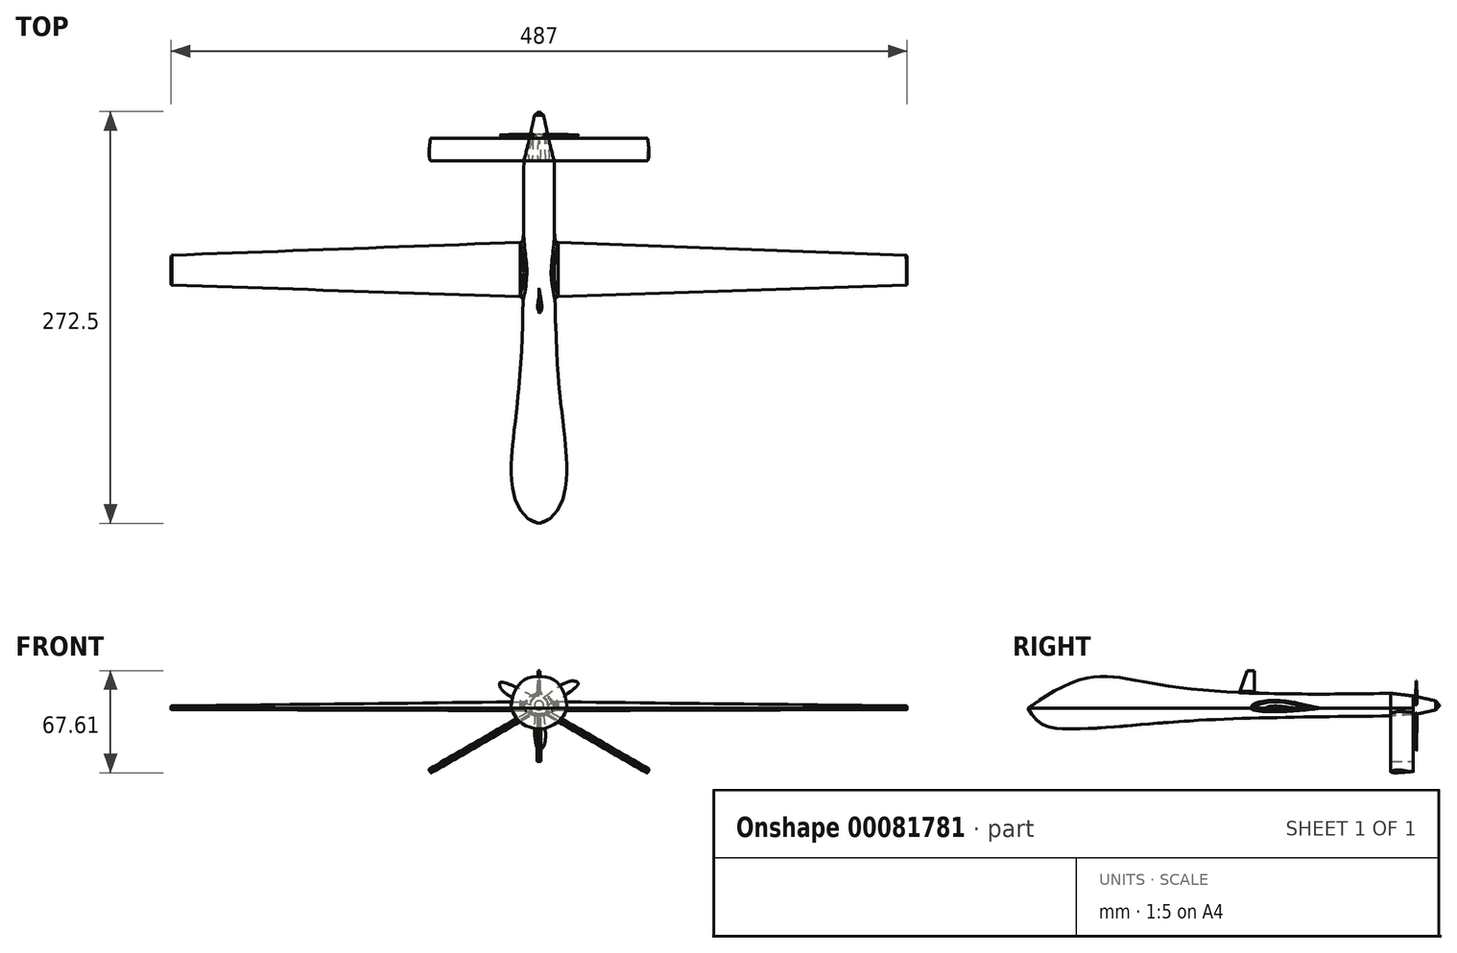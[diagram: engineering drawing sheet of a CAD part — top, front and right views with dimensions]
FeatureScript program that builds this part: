
annotation { "Feature Type Name" : "Feature", "Feature Type Description" : "" }
export const myFeature = defineFeature(function(context is Context, id is Id, definition is map)
    precondition{}
    {
        {
            var Q0;
            Q0=qCreatedBy(makeId("Right.planeOp"),FACE);
            var sketch = newSketch(context, id + "F0", { "sketchPlane" : qUnion([Q0])});
            skLineSegment(sketch, "E0", {"start": v(0, 0) * mm, "end": v(240, 0) * mm});
            skFitSpline(sketch, "E1", {"points": [v(0, 0) * mm, v(37.5, 19.82) * mm, v(94.65, 14.48) * mm, v(240, 10) * mm], "startDerivative": vector(93.49, 65.35) * mm, "endDerivative": vector(326.63, 5.9) * mm});
            skLineSegment(sketch, "E2", {"start": v(240, 10) * mm, "end": v(240, 0) * mm});
            skSolve(sketch);
        }
        {
            var Q0;
            Q0=qCreatedBy(makeId("Front.planeOp"),FACE);
            cPlane(context, id + "F1", {"entities" : qUnion([Q0]), "cplaneType" : CPlaneType.OFFSET, "offset" : 240 * mm, "oppositeDirection" : true, "width" : 150 * mm, "height" : 150 * mm});
        }
        {
            var Q0;
            Q0=qCreatedBy(id+"F1.planeOp",FACE);
            var sketch = newSketch(context, id + "F2", { "sketchPlane" : qUnion([Q0])});
            skArc(sketch, "E3", {"start": v(10, 0) * mm, "mid": v(0, 10) * mm, "end": v(-10, 0) * mm});
            skLineSegment(sketch, "E4", {"start": v(-10, 0) * mm, "end": v(10, 0) * mm});
            skPoint(sketch, "E5.0.start.orphan", {"position": v(0, 10) * mm});
            skSolve(sketch);
        }
        {
            var Q0;
            Q0=qCreatedBy(makeId("Top.planeOp"),FACE);
            var sketch = newSketch(context, id + "F3", { "sketchPlane" : qUnion([Q0])});
            skLineSegment(sketch, "E6", {"start": v(0, 0) * mm, "end": v(0, 272.56) * mm, "construction": true});
            skFitSpline(sketch, "E7.0", {"points": [v(0, 240) * mm, v(-3.33, 240) * mm, v(-6.67, 240) * mm, v(-10, 240) * mm]});
            skFitSpline(sketch, "E8", {"points": [v(-10, 240) * mm, v(-13.37, 88.04) * mm, v(-16.88, 19.92) * mm, v(0, 0) * mm], "startDerivative": vector(-2.86, -342.32) * mm, "endDerivative": vector(133.74, -24.52) * mm});
            skFitSpline(sketch, "E9.MirrorCS", {"points": [v(10, 240) * mm, v(13.37, 88.04) * mm, v(16.88, 19.92) * mm, v(0, 0) * mm], "startDerivative": vector(2.86, -342.32) * mm, "endDerivative": vector(-133.74, -24.52) * mm});
            skSolve(sketch);
        }
        {
            var Q0;
            Q0=qCreatedBy(makeId("Front.planeOp"),FACE);
            cPlane(context, id + "F4", {"entities" : qUnion([Q0]), "cplaneType" : CPlaneType.OFFSET, "offset" : 37.5 * mm, "oppositeDirection" : true, "width" : 150 * mm, "height" : 150 * mm});
        }
        {
            var Q0;
            Q0=qCreatedBy(id+"F4.planeOp",FACE);
            var sketch = newSketch(context, id + "F5", { "sketchPlane" : qUnion([Q0])});
            skArc(sketch, "E10", {"start": v(18.28, 0) * mm, "mid": v(0, 19.82) * mm, "end": v(-18.28, 0) * mm});
            skLineSegment(sketch, "E11", {"start": v(-18.28, 0) * mm, "end": v(18.28, 0) * mm});
            skSolve(sketch);
        }
        {
            var Q0;
            Q0=qCreatedBy(makeId("Front.planeOp"),FACE);
            cPlane(context, id + "F6", {"entities" : qUnion([Q0]), "cplaneType" : CPlaneType.OFFSET, "offset" : 150 * mm, "oppositeDirection" : true, "width" : 150 * mm, "height" : 150 * mm});
        }
        {
            var Q0;
            Q0=qCreatedBy(id+"F6.planeOp",FACE);
            var sketch = newSketch(context, id + "F7", { "sketchPlane" : qUnion([Q0])});
            skArc(sketch, "E12", {"start": v(10.54, 0) * mm, "mid": v(0, 10.12) * mm, "end": v(-10.54, 0) * mm});
            skLineSegment(sketch, "E13", {"start": v(-10.54, 0) * mm, "end": v(10.54, 0) * mm});
            skSolve(sketch);
        }
        {
            var Q0;
            Q0=makeQuery(id+"F2.imprint","IMPRINT",FACE,{"disambiguationData":[TD([[makeQuery(id+"F2.imprint","IMPRINT",EDGE,{"derivedFrom":sQuery(id+"F2.wireOp",EDGE,"E3")}),1.0]])]});
            var Q1;
            Q1=makeQuery(id+"F7.imprint","IMPRINT",FACE,{"disambiguationData":[TD([[makeQuery(id+"F7.imprint","IMPRINT",EDGE,{"derivedFrom":sQuery(id+"F7.wireOp",EDGE,"E12")}),1.0]])]});
            var Q2;
            Q2=makeQuery(id+"F5.imprint","IMPRINT",FACE,{"disambiguationData":[TD([[makeQuery(id+"F5.imprint","IMPRINT",EDGE,{"derivedFrom":sQuery(id+"F5.wireOp",EDGE,"E10")}),1.0]])]});
            var Q3;
            Q3=sQuery(id+"F3.wireOp",VERTEX,"E9.MirrorCS.3.internal");
            var Q4;
            Q4=sQuery(id+"F0.wireOp",EDGE,"E1");
            var Q5;
            Q5=sQuery(id+"F3.wireOp",EDGE,"E9.MirrorCS");
            var Q6;
            Q6=sQuery(id+"F3.wireOp",EDGE,"E8");
            loft(context, id + "F8", {"addGuides" : true, "sheetProfilesArray" : [{ "sheetProfileEntities" : qUnion([Q0]) }, { "sheetProfileEntities" : qUnion([Q1]) }, { "sheetProfileEntities" : qUnion([Q2]) }, { "sheetProfileEntities" : qUnion([Q3]) }], "guidesArray" : [{ "guideEntities" : qUnion([Q4]), "guideDerivativeType" : LoftGuideDerivativeType.DEFAULT, "guideDerivativeMagnitude" : 1 }, { "guideEntities" : qUnion([Q5]), "guideDerivativeType" : LoftGuideDerivativeType.DEFAULT, "guideDerivativeMagnitude" : 1 }, { "guideEntities" : qUnion([Q6]), "guideDerivativeType" : LoftGuideDerivativeType.DEFAULT, "guideDerivativeMagnitude" : 1 }]});
        }
        {
            var Q0;
            Q0=qCreatedBy(makeId("Right.planeOp"),FACE);
            var sketch = newSketch(context, id + "F9", { "sketchPlane" : qUnion([Q0])});
            skPoint(sketch, "E14.0", {"position": v(240, 0) * mm});
            skFitSpline(sketch, "E15", {"points": [v(0, 0) * mm, v(16.5, -12.8) * mm, v(84.8, -9.9) * mm, v(240, -5) * mm], "startDerivative": vector(89.7, -143.98) * mm, "endDerivative": vector(544.57, 5.36) * mm});
            skLineSegment(sketch, "E16", {"start": v(0, 0) * mm, "end": v(240, 0) * mm});
            skSolve(sketch);
        }
        {
            var Q0;
            Q0=qCreatedBy(id+"F1.planeOp",FACE);
            var sketch = newSketch(context, id + "F10", { "sketchPlane" : qUnion([Q0])});
            skFitSpline(sketch, "E17.0", {"points": [v(0, 0) * mm, v(-3.33, 0) * mm, v(-6.67, 0) * mm, v(-10, 0) * mm]});
            skLineSegment(sketch, "E18.0", {"start": v(-10, 0) * mm, "end": v(10, 0) * mm});
            skArc(sketch, "E19", {"start": v(-10, 0) * mm, "mid": v(0, -5) * mm, "end": v(10, 0) * mm});
            skSolve(sketch);
        }
        {
            var Q0;
            Q0=qCreatedBy(id+"F6.planeOp",FACE);
            var sketch = newSketch(context, id + "F11", { "sketchPlane" : qUnion([Q0])});
            skArc(sketch, "E20", {"start": v(-10.54, 0) * mm, "mid": v(0, -6.4) * mm, "end": v(10.54, 0) * mm});
            skLineSegment(sketch, "E21", {"start": v(10.54, 0) * mm, "end": v(-10.54, 0) * mm});
            skSolve(sketch);
        }
        {
            var Q0;
            Q0=qCreatedBy(id+"F4.planeOp",FACE);
            var sketch = newSketch(context, id + "F12", { "sketchPlane" : qUnion([Q0])});
            skArc(sketch, "E22", {"start": v(-18.28, 0) * mm, "mid": v(0, -13.44) * mm, "end": v(18.28, 0) * mm});
            skLineSegment(sketch, "E23", {"start": v(-18.28, 0) * mm, "end": v(18.28, 0) * mm});
            skSolve(sketch);
        }
        {
            var Q1;
            {var subQ0=sQuery(id+"F10.wireOp",EDGE,"E19");Q1=makeQuery(id+"F10.imprint","IMPRINT",FACE,{"disambiguationData":[TD([[makeQuery(id+"F10.imprint","IMPRINT",EDGE,{"derivedFrom":subQ0}),1.0]])]});}
            var Q2;
            Q2=makeQuery(id+"F11.imprint","IMPRINT",FACE,{"disambiguationData":[TD([[makeQuery(id+"F11.imprint","IMPRINT",EDGE,{"derivedFrom":sQuery(id+"F11.wireOp",EDGE,"E20")}),1.0]])]});
            var Q3;
            Q3=makeQuery(id+"F12.imprint","IMPRINT",FACE,{"disambiguationData":[TD([[makeQuery(id+"F12.imprint","IMPRINT",EDGE,{"derivedFrom":sQuery(id+"F12.wireOp",EDGE,"E22")}),1.0]])]});
            var Q4;
            Q4=sQuery(id+"F9.wireOp",VERTEX,"E15.0.internal");
            var Q5;
            Q5=sQuery(id+"F3.wireOp",EDGE,"E8");
            var Q6;
            Q6=sQuery(id+"F3.wireOp",EDGE,"E9.MirrorCS");
            var Q7;
            Q7=sQuery(id+"F9.wireOp",EDGE,"E15");
            loft(context, id + "F13", {"operationType" : NewBodyOperationType.ADD, "addGuides" : true, "sheetProfilesArray" : [{ "sheetProfileEntities" : qUnion([Q1]) }, { "sheetProfileEntities" : qUnion([Q2]) }, { "sheetProfileEntities" : qUnion([Q3]) }, { "sheetProfileEntities" : qUnion([Q4]) }], "guidesArray" : [{ "guideEntities" : qUnion([Q5]), "guideDerivativeType" : LoftGuideDerivativeType.DEFAULT, "guideDerivativeMagnitude" : 1 }, { "guideEntities" : qUnion([Q6]), "guideDerivativeType" : LoftGuideDerivativeType.DEFAULT, "guideDerivativeMagnitude" : 1 }, { "guideEntities" : qUnion([Q7]), "guideDerivativeType" : LoftGuideDerivativeType.DEFAULT, "guideDerivativeMagnitude" : 1 }]});
        }
        {
            var Q0;
            Q0=qCreatedBy(makeId("Right.planeOp"),FACE);
            var sketch = newSketch(context, id + "F14", { "sketchPlane" : qUnion([Q0])});
            skLineSegment(sketch, "E24", {"start": v(0, 0) * mm, "end": v(150, 0) * mm, "construction": true});
            skLineSegment(sketch, "E25", {"start": v(150, 0) * mm, "end": v(186, 0) * mm, "construction": true});
            skFitSpline(sketch, "E26", {"points": [v(150, 0) * mm, v(162.77, 4.35) * mm, v(186, 0) * mm], "startDerivative": vector(1.89, 17.28) * mm, "endDerivative": vector(43.95, -12.7) * mm});
            skFitSpline(sketch, "E27", {"points": [v(150, 0) * mm, v(161.94, -1.41) * mm, v(186, 0) * mm], "startDerivative": vector(11.14, -7.95) * mm, "endDerivative": vector(52.3, 6.57) * mm});
            skSolve(sketch);
        }
        {
            var Q0;
            Q0 = qSketchRegion(id + "F14", true);
            extrude(context, id + "F15", {"entities" : qUnion([Q0]), "operationType" : NewBodyOperationType.ADD, "endBound" : BoundingType.SYMMETRIC, "depth" : 25 * mm});
        }
        {
            var Q0;
            Q0=qCreatedBy(makeId("Right.planeOp"),FACE);
            cPlane(context, id + "F16", {"entities" : qUnion([Q0]), "cplaneType" : CPlaneType.OFFSET, "offset" : 243.5 * mm, "width" : 150 * mm, "height" : 150 * mm});
        }
        {
            var Q0;
            Q0=qCreatedBy(id+"F16.planeOp",FACE);
            var sketch = newSketch(context, id + "F17", { "sketchPlane" : qUnion([Q0])});
            skFitSpline(sketch, "E28.0.0", {"points": [v(186, 0) * mm, v(177.65, 2.41) * mm, v(165.41, 6.33) * mm, v(150.27, 2.48) * mm, v(150, 0) * mm]});
            skFitSpline(sketch, "E28.0.1", {"points": [v(150, 0) * mm, v(151.54, -1.1) * mm, v(164.41, -1.68) * mm, v(175.78, -1.28) * mm, v(186, 0) * mm]});
            skLineSegment(sketch, "E29", {"start": v(142.65, 0) * mm, "end": v(197.39, 0) * mm, "construction": true});
            skFitSpline(sketch, "E30", {"points": [v(157.7, 0) * mm, v(162.9, 1.58) * mm, v(177.41, 0) * mm], "startDerivative": vector(0.8, 8.3) * mm, "endDerivative": vector(32.19, -4.29) * mm});
            skFitSpline(sketch, "E31", {"points": [v(157.7, 0) * mm, v(164.23, -0.7) * mm, v(177.41, 0) * mm], "startDerivative": vector(2.27, -4.37) * mm, "endDerivative": vector(24.46, 2.77) * mm});
            skSolve(sketch);
        }
        {
            var Q0;
            Q0=makeQuery(id+"F17.imprint","IMPRINT",FACE,{"disambiguationData":[TD([[makeQuery(id+"F17.imprint","IMPRINT",EDGE,{"derivedFrom":sQuery(id+"F17.wireOp",EDGE,"E30")}),-1.0]])]});
            var Q1;
            Q1=makeQuery(id+"F15.opExtrude","CAP_FACE",FACE,{"disambiguationData":[OSD([sQuery(id+"F14.wireOp",EDGE,"E26"),sQuery(id+"F14.wireOp",EDGE,"E27")])],"isStart":false});
            loft(context, id + "F18", {"sheetProfilesArray" : [{ "sheetProfileEntities" : qUnion([Q0]) }, { "sheetProfileEntities" : qUnion([Q1]) }]});
        }
        {
            var Q0;
            {var subQ0=sQuery(id+"F17.wireOp",EDGE,"E30");var subQ1=sQuery(id+"F17.wireOp",EDGE,"E31");Q0=makeQuery(id+"F18.opLoft","MID_CAP_EDGE",EDGE,{"disambiguationData":[OSD([subQ0,subQ1]),TDD([makeQuery(id+"F17.imprint","INTERSECT",VERTEX,{"disambiguationData":[OD(0.0)],"derivedFrom":[subQ0,subQ1]}),makeQuery(id+"F17.imprint","INTERSECT",VERTEX,{"disambiguationData":[OD(1.0)],"derivedFrom":[subQ0,subQ1]}),makeQuery(id+"F17.imprint","IMPRINT",EDGE,{"derivedFrom":subQ0})])],"capPos":0.0});}
            fillet(context, id + "F19", {"entities" : qUnion([Q0]), "radius" : 0.5 * mm, "tangentPropagation" : true, "allowEdgeOverflow" : false});
        }
        {
            var Q0;
            Q0=makeQuery(id+"F18.opLoft","SWEPT_BODY",BODY,{"disambiguationData":[OSD([sQuery(id+"F14.wireOp",EDGE,"E26"),sQuery(id+"F14.wireOp",EDGE,"E27"),makeQuery(id+"F17.imprint","IMPRINT",FACE,{"disambiguationData":[TD([[makeQuery(id+"F17.imprint","IMPRINT",EDGE,{"derivedFrom":sQuery(id+"F17.wireOp",EDGE,"E30")}),-1.0]])]})])]});
            var Q1;
            Q1=qCreatedBy(makeId("Right.planeOp"),FACE);
            mirror(context, id + "F20", {"operationType" : NewBodyOperationType.ADD, "entities" : qUnion([Q0]), "mirrorPlane" : qUnion([Q1])});
        }
        {
            var Q0;
            Q0=qCreatedBy(makeId("Front.planeOp"),FACE);
            cPlane(context, id + "F21", {"entities" : qUnion([Q0]), "cplaneType" : CPlaneType.OFFSET, "offset" : 255 * mm, "oppositeDirection" : true, "width" : 150 * mm, "height" : 150 * mm});
        }
        {
            var Q0;
            Q0=qCreatedBy(id+"F21.planeOp",FACE);
            var sketch = newSketch(context, id + "F22", { "sketchPlane" : qUnion([Q0])});
            skFitSpline(sketch, "E32.0.0", {"points": [v(0, 10) * mm, v(0.66, 10) * mm, v(1.3, 9.94) * mm, v(1.95, 9.8) * mm, v(2.6, 9.68) * mm, v(3.22, 9.5) * mm, v(3.83, 9.24) * mm, v(4.43, 8.99) * mm, v(5, 8.68) * mm, v(5.56, 8.31) * mm, v(6.1, 7.95) * mm, v(6.6, 7.54) * mm, v(7.07, 7.07) * mm, v(7.53, 6.6) * mm, v(7.95, 6.1) * mm, v(8.31, 5.56) * mm, v(8.68, 5.01) * mm, v(8.99, 4.43) * mm, v(9.24, 3.83) * mm, v(9.49, 3.22) * mm, v(9.68, 2.6) * mm, v(9.8, 1.95) * mm, v(9.94, 1.3) * mm, v(10, 0.66) * mm, v(10, 0) * mm]});
            skFitSpline(sketch, "E32.0.1", {"points": [v(10, 0) * mm, v(9.42, -0.78) * mm, v(8.75, -1.47) * mm, v(8, -2.1) * mm, v(7.27, -2.72) * mm, v(6.46, -3.25) * mm, v(5.6, -3.68) * mm, v(4.72, -4.11) * mm, v(3.82, -4.44) * mm, v(2.87, -4.67) * mm, v(1.93, -4.89) * mm, v(0.97, -5) * mm, v(0, -5) * mm]});
            skFitSpline(sketch, "E32.0.2", {"points": [v(0, -5) * mm, v(-0.97, -5) * mm, v(-1.93, -4.89) * mm, v(-2.87, -4.67) * mm, v(-3.82, -4.44) * mm, v(-4.72, -4.11) * mm, v(-5.6, -3.68) * mm, v(-6.46, -3.25) * mm, v(-7.26, -2.72) * mm, v(-8, -2.1) * mm, v(-8.75, -1.48) * mm, v(-9.42, -0.78) * mm, v(-10, 0) * mm]});
            skFitSpline(sketch, "E32.0.3", {"points": [v(-10, 0) * mm, v(-10, 0.66) * mm, v(-9.94, 1.3) * mm, v(-9.8, 1.95) * mm, v(-9.68, 2.6) * mm, v(-9.5, 3.22) * mm, v(-9.24, 3.83) * mm, v(-8.99, 4.43) * mm, v(-8.68, 5) * mm, v(-8.31, 5.56) * mm, v(-7.95, 6.1) * mm, v(-7.54, 6.6) * mm, v(-7.07, 7.07) * mm, v(-6.6, 7.53) * mm, v(-6.1, 7.95) * mm, v(-5.56, 8.31) * mm, v(-5.01, 8.68) * mm, v(-4.43, 8.99) * mm, v(-3.83, 9.24) * mm, v(-3.22, 9.49) * mm, v(-2.6, 9.68) * mm, v(-1.95, 9.8) * mm, v(-1.3, 9.94) * mm, v(-0.66, 10) * mm, v(0, 10) * mm]});
            skCircle(sketch, "E33", {"center": v(0, 2) * mm, "radius": 6.25 * mm});
            skLineSegment(sketch, "E34", {"start": v(10, 0) * mm, "end": v(-10, 0) * mm, "construction": true});
            skPoint(sketch, "E35", {"position": v(5.92, 0) * mm});
            skPoint(sketch, "E36", {"position": v(-5.92, 0) * mm});
            skPoint(sketch, "E37", {"position": v(0, 8.25) * mm});
            skPoint(sketch, "E38", {"position": v(0, -4.25) * mm});
            skSolve(sketch);
        }
        {
            var Q0;
            Q0=qCreatedBy(makeId("Front.planeOp"),FACE);
            cPlane(context, id + "F23", {"entities" : qUnion([Q0]), "cplaneType" : CPlaneType.OFFSET, "offset" : 270 * mm, "oppositeDirection" : true, "width" : 150 * mm, "height" : 150 * mm});
        }
        {
            var Q0;
            Q0=qCreatedBy(makeId("Top.planeOp"),FACE);
            var sketch = newSketch(context, id + "F24", { "sketchPlane" : qUnion([Q0])});
            skPoint(sketch, "E39.0", {"position": v(-10, 240) * mm});
            skPoint(sketch, "E40.0", {"position": v(10, 240) * mm});
            skPoint(sketch, "E41.0", {"position": v(-5.92, 255) * mm});
            skPoint(sketch, "E42.0", {"position": v(5.92, 255) * mm});
            skLineSegment(sketch, "E43", {"start": v(10, 240) * mm, "end": v(5.92, 255) * mm});
            skLineSegment(sketch, "E44", {"start": v(-10, 240) * mm, "end": v(-5.92, 255) * mm});
            skSolve(sketch);
        }
        {
            var Q1;
            {var subQ0=sQuery(id+"F10.wireOp",EDGE,"E19");Q1=makeQuery(id+"F13.boolean.opBoolean","MERGE",FACE,{"derivedFrom":[makeQuery(id+"F8.opLoft","CAP_FACE",FACE,{"disambiguationData":[OSD([makeQuery(id+"F2.imprint","IMPRINT",FACE,{"disambiguationData":[TD([[makeQuery(id+"F2.imprint","IMPRINT",EDGE,{"derivedFrom":sQuery(id+"F2.wireOp",EDGE,"E3")}),1.0]])]})])],"isStart":true}),makeQuery(id+"F13.opLoft","CAP_FACE",FACE,{"disambiguationData":[OSD([makeQuery(id+"F10.imprint","IMPRINT",FACE,{"disambiguationData":[TD([[makeQuery(id+"F10.imprint","IMPRINT",EDGE,{"derivedFrom":subQ0}),1.0]])]})])],"isStart":true})]});}
            var Q2;
            Q2=makeQuery(id+"F22.imprint","IMPRINT",FACE,{"disambiguationData":[TD([[makeQuery(id+"F22.imprint","IMPRINT",EDGE,{"derivedFrom":sQuery(id+"F22.wireOp",EDGE,"E33")}),1.0]])]});
            var Q3;
            Q3=sQuery(id+"F24.wireOp",EDGE,"E44");
            var Q4;
            Q4=sQuery(id+"F24.wireOp",EDGE,"E43");
            loft(context, id + "F25", {"operationType" : NewBodyOperationType.ADD, "addGuides" : true, "sheetProfilesArray" : [{ "sheetProfileEntities" : qUnion([Q1]) }, { "sheetProfileEntities" : qUnion([Q2]) }], "guidesArray" : [{ "guideEntities" : qUnion([Q3]), "guideDerivativeType" : LoftGuideDerivativeType.DEFAULT, "guideDerivativeMagnitude" : 1 }, { "guideEntities" : qUnion([Q4]), "guideDerivativeType" : LoftGuideDerivativeType.DEFAULT, "guideDerivativeMagnitude" : 1 }]});
        }
        {
            var Q0;
            Q0=qCreatedBy(id+"F23.planeOp",FACE);
            var sketch = newSketch(context, id + "F26", { "sketchPlane" : qUnion([Q0])});
            skCircle(sketch, "E45", {"center": v(0, 2) * mm, "radius": 3 * mm});
            skSolve(sketch);
        }
        {
            var Q1;
            Q1=makeQuery(id+"F25.opLoft","CAP_FACE",FACE,{"disambiguationData":[OSD([makeQuery(id+"F22.imprint","IMPRINT",FACE,{"disambiguationData":[TD([[makeQuery(id+"F22.imprint","IMPRINT",EDGE,{"derivedFrom":sQuery(id+"F22.wireOp",EDGE,"E33")}),1.0]])]})])],"isStart":true});
            var Q2;
            Q2=makeQuery(id+"F26.imprint","IMPRINT",FACE,{"disambiguationData":[TD([[makeQuery(id+"F26.imprint","IMPRINT",EDGE,{"derivedFrom":sQuery(id+"F26.wireOp",EDGE,"E45")}),1.0]])]});
            loft(context, id + "F27", {"operationType" : NewBodyOperationType.ADD, "sheetProfilesArray" : [{ "sheetProfileEntities" : qUnion([Q1]) }, { "sheetProfileEntities" : qUnion([Q2]) }]});
        }
        {
            var Q0;
            Q0=qCreatedBy(makeId("Front.planeOp"),FACE);
            cPlane(context, id + "F28", {"entities" : qUnion([Q0]), "cplaneType" : CPlaneType.OFFSET, "offset" : 272.5 * mm, "oppositeDirection" : true, "width" : 150 * mm, "height" : 150 * mm});
        }
        {
            var Q0;
            Q0=qCreatedBy(id+"F28.planeOp",FACE);
            var sketch = newSketch(context, id + "F29", { "sketchPlane" : qUnion([Q0])});
            skFitSpline(sketch, "E46.0.0", {"points": [v(3, 2) * mm, v(3, 1.6) * mm, v(2.92, 1.22) * mm, v(2.77, 0.85) * mm, v(2.62, 0.49) * mm, v(2.4, 0.16) * mm, v(2.12, -0.12) * mm, v(1.84, -0.4) * mm, v(1.52, -0.62) * mm, v(1.15, -0.77) * mm, v(0.78, -0.92) * mm, v(0.4, -1) * mm, v(0, -1) * mm]});
            skFitSpline(sketch, "E46.0.1", {"points": [v(0, -1) * mm, v(-0.4, -1) * mm, v(-0.78, -0.92) * mm, v(-1.15, -0.77) * mm, v(-1.51, -0.62) * mm, v(-1.84, -0.4) * mm, v(-2.12, -0.12) * mm, v(-2.4, 0.16) * mm, v(-2.62, 0.48) * mm, v(-2.77, 0.85) * mm, v(-2.92, 1.22) * mm, v(-3, 1.6) * mm, v(-3, 2) * mm]});
            skFitSpline(sketch, "E46.0.2", {"points": [v(-3, 2) * mm, v(-3, 2.4) * mm, v(-2.92, 2.78) * mm, v(-2.77, 3.15) * mm, v(-2.62, 3.51) * mm, v(-2.4, 3.84) * mm, v(-2.12, 4.12) * mm, v(-1.84, 4.4) * mm, v(-1.52, 4.62) * mm, v(-1.15, 4.77) * mm, v(-0.78, 4.92) * mm, v(-0.4, 5) * mm, v(0, 5) * mm]});
            skFitSpline(sketch, "E46.0.3", {"points": [v(0, 5) * mm, v(0.4, 5) * mm, v(0.78, 4.92) * mm, v(1.15, 4.77) * mm, v(1.51, 4.62) * mm, v(1.84, 4.4) * mm, v(2.12, 4.12) * mm, v(2.4, 3.84) * mm, v(2.62, 3.52) * mm, v(2.77, 3.15) * mm, v(2.92, 2.78) * mm, v(3, 2.4) * mm, v(3, 2) * mm]});
            skPoint(sketch, "E47", {"position": v(0, 2) * mm});
            skSolve(sketch);
        }
        {
            var Q1;
            Q1=makeQuery(id+"F27.opLoft","CAP_FACE",FACE,{"disambiguationData":[OSD([makeQuery(id+"F26.imprint","IMPRINT",FACE,{"disambiguationData":[TD([[makeQuery(id+"F26.imprint","IMPRINT",EDGE,{"derivedFrom":sQuery(id+"F26.wireOp",EDGE,"E45")}),1.0]])]})])],"isStart":true});
            var Q2;
            Q2=sQuery(id+"F29.wireOp",VERTEX,"E47");
            loft(context, id + "F30", {"operationType" : NewBodyOperationType.ADD, "sheetProfilesArray" : [{ "sheetProfileEntities" : qUnion([Q1]) }, { "sheetProfileEntities" : qUnion([Q2]) }]});
        }
        {
            var Q0;
            Q0=qCreatedBy(makeId("Right.planeOp"),FACE);
            cPlane(context, id + "F31", {"entities" : qUnion([Q0]), "cplaneType" : CPlaneType.OFFSET, "offset" : 72 * mm, "width" : 150 * mm, "height" : 150 * mm});
        }
        {
            var Q0;
            Q0=qCreatedBy(id+"F31.planeOp",FACE);
            var sketch = newSketch(context, id + "F32", { "sketchPlane" : qUnion([Q0])});
            skLineSegment(sketch, "E48", {"start": v(0, 0) * mm, "end": v(0, -42) * mm, "construction": true});
            skLineSegment(sketch, "E49", {"start": v(0, -42) * mm, "end": v(271.23, -42) * mm});
            skSolve(sketch);
        }
        {
            assignVariable(context, id + "F33", {"name" : "angle", "anyValue" : 120});
        }
        {
            var Q0;
            Q0=sQuery(id+"F32.wireOp",EDGE,"E49");
            cPlane(context, id + "F34", {"entities" : qUnion([Q0]), "cplaneType" : CPlaneType.LINE_ANGLE, "offset" : 150 * mm, "angle" : (getVariable(context, 'angle')) * degree, "width" : 150 * mm, "height" : 150 * mm});
        }
        {
            var Q0;
            Q0=qCreatedBy(id+"F34.planeOp",FACE);
            var sketch = newSketch(context, id + "F35", { "sketchPlane" : qUnion([Q0])});
            skFitSpline(sketch, "E50.0", {"points": [v(240, 5) * mm, v(245, 4.32) * mm, v(250, 3.64) * mm, v(255, 2.96) * mm], "construction": true});
            skLineSegment(sketch, "E51.0", {"start": v(0, -0.37) * mm, "end": v(242.6, -0.37) * mm, "construction": true});
            skPoint(sketch, "E52.orphan", {"position": v(271.23, -0.37) * mm});
            skFitSpline(sketch, "E53", {"points": [v(240, -0.37) * mm, v(244.56, 1.55) * mm, v(255, -0.37) * mm], "startDerivative": vector(6.04, 10.7) * mm, "endDerivative": vector(29.02, -7.53) * mm});
            skFitSpline(sketch, "E54", {"points": [v(240, -0.37) * mm, v(244.42, -1.27) * mm, v(255, -0.37) * mm], "startDerivative": vector(3.63, -7.22) * mm, "endDerivative": vector(30.34, 2.29) * mm});
            skSolve(sketch);
        }
        {
            var Q0;
            Q0=makeQuery(id+"F35.imprint","IMPRINT",FACE,{"disambiguationData":[TD([[makeQuery(id+"F35.imprint","IMPRINT",EDGE,{"derivedFrom":sQuery(id+"F35.wireOp",EDGE,"E53")}),-1.0]])]});
            extrude(context, id + "F36", {"entities" : qUnion([Q0]), "oppositeDirection" : true, "depth" : 80 * mm});
        }
        {
            var Q0;
            Q0=makeQuery(id+"F36.opExtrude","CAP_EDGE",EDGE,{"disambiguationData":[OSD([sQuery(id+"F35.wireOp",EDGE,"E53")])],"isStart":true});
            var Q1;
            Q1=makeQuery(id+"F36.opExtrude","CAP_EDGE",EDGE,{"disambiguationData":[OSD([sQuery(id+"F35.wireOp",EDGE,"E54")])],"isStart":true});
            fillet(context, id + "F37", {"entities" : qUnion([Q0, Q1]), "radius" : 0.5 * mm, "tangentPropagation" : true, "allowEdgeOverflow" : false});
        }
        {
            var Q0;
            Q0=makeQuery(id+"F36.opExtrude","SWEPT_BODY",BODY,{"disambiguationData":[OSD([sQuery(id+"F35.wireOp",EDGE,"E53"),sQuery(id+"F35.wireOp",EDGE,"E54")])]});
            var Q1;
            Q1=qCreatedBy(makeId("Right.planeOp"),FACE);
            mirror(context, id + "F38", {"operationType" : NewBodyOperationType.ADD, "entities" : qUnion([Q0]), "mirrorPlane" : qUnion([Q1])});
        }
        {
            var Q0;
            Q0=qCreatedBy(makeId("Top.planeOp"),FACE);
            var sketch = newSketch(context, id + "F39", { "sketchPlane" : qUnion([Q0])});
            skLineSegment(sketch, "E55", {"start": v(0, 0) * mm, "end": v(0, 257) * mm, "construction": true});
            skEllipse(sketch, "E56", {"center": v(0, 257) * mm, "majorRadius": 2.5 * mm, "minorRadius": 0.6 * mm, "majorAxis": v(-1, 0)});
            skSolve(sketch);
        }
        {
            var Q0;
            Q0=qCreatedBy(makeId("Front.planeOp"),FACE);
            cPlane(context, id + "F40", {"entities" : qUnion([Q0]), "cplaneType" : CPlaneType.OFFSET, "offset" : 257 * mm, "oppositeDirection" : true, "width" : 150 * mm, "height" : 150 * mm});
        }
        {
            var Q0;
            Q0=qCreatedBy(id+"F40.planeOp",FACE);
            var sketch = newSketch(context, id + "F41", { "sketchPlane" : qUnion([Q0])});
            skLineSegment(sketch, "E57.0", {"start": v(2.5, 0) * mm, "end": v(-2.5, 0) * mm});
            skLineSegment(sketch, "E58", {"start": v(0, 0) * mm, "end": v(0, -28) * mm, "construction": true});
            skFitSpline(sketch, "E59", {"points": [v(2.5, 0) * mm, v(4.19, -20.46) * mm, v(0, -28) * mm], "startDerivative": vector(5.82, -52.04) * mm, "endDerivative": vector(-22.98, -9.89) * mm});
            skFitSpline(sketch, "E60", {"points": [v(-2.5, 0) * mm, v(-2.5, -20.53) * mm, v(0, -28) * mm], "startDerivative": vector(-3.63, -41.05) * mm, "endDerivative": vector(9.75, -1.43) * mm});
            skSolve(sketch);
        }
        {
            var Q1;
            Q1=makeQuery(id+"F39.imprint","IMPRINT",FACE,{"disambiguationData":[TD([[makeQuery(id+"F39.imprint","IMPRINT",EDGE,{"derivedFrom":sQuery(id+"F39.wireOp",EDGE,"E56")}),1.0]])]});
            var Q2;
            Q2=sQuery(id+"F41.wireOp",VERTEX,"E60.end");
            var Q3;
            Q3=sQuery(id+"F41.wireOp",EDGE,"E59");
            var Q4;
            Q4=sQuery(id+"F41.wireOp",EDGE,"E60");
            loft(context, id + "F42", {"addGuides" : true, "sheetProfilesArray" : [{ "sheetProfileEntities" : qUnion([Q1]) }, { "sheetProfileEntities" : qUnion([Q2]) }], "guidesArray" : [{ "guideEntities" : qUnion([Q3]), "guideDerivativeType" : LoftGuideDerivativeType.DEFAULT, "guideDerivativeMagnitude" : 1 }, { "guideEntities" : qUnion([Q4]), "guideDerivativeType" : LoftGuideDerivativeType.DEFAULT, "guideDerivativeMagnitude" : 1 }]});
        }
        {
            var Q0;
            Q0=qCreatedBy(makeId("Top.planeOp"),FACE);
            cPlane(context, id + "F43", {"entities" : qUnion([Q0]), "cplaneType" : CPlaneType.OFFSET, "offset" : 2 * mm, "width" : 150 * mm, "height" : 150 * mm});
        }
        {
            var Q0;
            Q0=qCreatedBy(id+"F43.planeOp",FACE);
            var sketch = newSketch(context, id + "F44", { "sketchPlane" : qUnion([Q0])});
            skLineSegment(sketch, "E61", {"start": v(0, 0) * mm, "end": v(0, 416.26) * mm, "construction": true});
            skSolve(sketch);
        }
        {
            var Q0;
            Q0=makeQuery(id+"F42.opLoft","SWEPT_BODY",BODY,{"disambiguationData":[OSD([makeQuery(id+"F39.imprint","IMPRINT",FACE,{"disambiguationData":[TD([[makeQuery(id+"F39.imprint","IMPRINT",EDGE,{"derivedFrom":sQuery(id+"F39.wireOp",EDGE,"E56")}),1.0]])]}),sQuery(id+"F41.wireOp",VERTEX,"E60.end"),sQuery(id+"F41.wireOp",EDGE,"E59"),sQuery(id+"F41.wireOp",EDGE,"E60")])]});
            var Q1;
            Q1=sQuery(id+"F44.wireOp",EDGE,"E61");
            circularPattern(context, id + "F45", {"operationType" : NewBodyOperationType.ADD, "entities" : qUnion([Q0]), "axis" : qUnion([Q1]), "angle" : 120 * degree, "instanceCount" : 3});
        }
        {
            var Q0;
            Q0=makeQuery(id+"F15.boolean.opBoolean","INTERSECT",EDGE,{"disambiguationData":[OD(1.0)],"derivedFrom":[makeQuery(id+"F13.opLoft","SWEPT_FACE",FACE,{"disambiguationData":[OSD([sQuery(id+"F3.wireOp",EDGE,"E8"),sQuery(id+"F9.wireOp",EDGE,"E15"),sQuery(id+"F10.wireOp",EDGE,"E19"),sQuery(id+"F11.wireOp",EDGE,"E20"),sQuery(id+"F12.wireOp",EDGE,"E22")])]}),makeQuery(id+"F15.opExtrude","SWEPT_FACE",FACE,{"disambiguationData":[OSD([sQuery(id+"F14.wireOp",EDGE,"E27")])]})]});
            var Q1;
            Q1=makeQuery(id+"F15.boolean.opBoolean","INTERSECT",EDGE,{"disambiguationData":[OD(0.0)],"derivedFrom":[makeQuery(id+"F13.opLoft","SWEPT_FACE",FACE,{"disambiguationData":[OSD([sQuery(id+"F3.wireOp",EDGE,"E8"),sQuery(id+"F9.wireOp",EDGE,"E15"),sQuery(id+"F10.wireOp",EDGE,"E19"),sQuery(id+"F11.wireOp",EDGE,"E20"),sQuery(id+"F12.wireOp",EDGE,"E22")])]}),makeQuery(id+"F15.opExtrude","SWEPT_FACE",FACE,{"disambiguationData":[OSD([sQuery(id+"F14.wireOp",EDGE,"E27")])]})]});
            var Q2;
            Q2=makeQuery(id+"F15.boolean.opBoolean","INTERSECT",EDGE,{"disambiguationData":[OD(1.0)],"derivedFrom":[makeQuery(id+"F8.opLoft","SWEPT_FACE",FACE,{"disambiguationData":[OSD([sQuery(id+"F0.wireOp",EDGE,"E1"),sQuery(id+"F2.wireOp",EDGE,"E3"),sQuery(id+"F3.wireOp",EDGE,"E9.MirrorCS"),sQuery(id+"F5.wireOp",EDGE,"E10"),sQuery(id+"F7.wireOp",EDGE,"E12")])]}),makeQuery(id+"F15.opExtrude","SWEPT_FACE",FACE,{"disambiguationData":[OSD([sQuery(id+"F14.wireOp",EDGE,"E26")])]})]});
            var Q3;
            Q3=makeQuery(id+"F15.boolean.opBoolean","INTERSECT",EDGE,{"disambiguationData":[OD(0.0)],"derivedFrom":[makeQuery(id+"F8.opLoft","SWEPT_FACE",FACE,{"disambiguationData":[OSD([sQuery(id+"F0.wireOp",EDGE,"E1"),sQuery(id+"F2.wireOp",EDGE,"E3"),sQuery(id+"F3.wireOp",EDGE,"E9.MirrorCS"),sQuery(id+"F5.wireOp",EDGE,"E10"),sQuery(id+"F7.wireOp",EDGE,"E12")])]}),makeQuery(id+"F15.opExtrude","SWEPT_FACE",FACE,{"disambiguationData":[OSD([sQuery(id+"F14.wireOp",EDGE,"E26")])]})]});
            fillet(context, id + "F46", {"entities" : qUnion([Q0, Q1, Q2, Q3]), "radius" : 2.5 * mm, "tangentPropagation" : true, "allowEdgeOverflow" : false});
        }
        {
            var Q0;
            Q0=qCreatedBy(makeId("Top.planeOp"),FACE);
            cPlane(context, id + "F47", {"entities" : qUnion([Q0]), "cplaneType" : CPlaneType.OFFSET, "offset" : 35 * mm, "oppositeDirection" : true, "width" : 150 * mm, "height" : 150 * mm});
        }
        {
            var Q0;
            Q0=qCreatedBy(id+"F47.planeOp",FACE);
            var sketch = newSketch(context, id + "F48", { "sketchPlane" : qUnion([Q0])});
            skLineSegment(sketch, "E62", {"start": v(0, 0) * mm, "end": v(0, 240) * mm, "construction": true});
            skFitSpline(sketch, "E63", {"points": [v(0, 240) * mm, v(-1.2, 243.6) * mm, v(0, 255) * mm], "startDerivative": vector(-6.2, 2.4) * mm, "endDerivative": vector(4.32, 22.5) * mm});
            skFitSpline(sketch, "E64.MirrorCS", {"points": [v(0, 240) * mm, v(1.2, 243.6) * mm, v(0, 255) * mm], "startDerivative": vector(6.2, 2.4) * mm, "endDerivative": vector(-4.32, 22.5) * mm});
            skSolve(sketch);
        }
        {
            var Q0;
            Q0=makeQuery(id+"F48.imprint","IMPRINT",FACE,{"disambiguationData":[TD([[makeQuery(id+"F48.imprint","IMPRINT",EDGE,{"derivedFrom":sQuery(id+"F48.wireOp",EDGE,"E63")}),-1.0]])]});
            var Q1;
            {var subQ0=makeQuery(id+"F36.opExtrude","SWEPT_FACE",FACE,{"disambiguationData":[OSD([sQuery(id+"F35.wireOp",EDGE,"E53")])]});var subQ1=sQuery(id+"F24.wireOp",EDGE,"E43");var subQ2=sQuery(id+"F22.wireOp",EDGE,"E33");var subQ3=sQuery(id+"F10.wireOp",EDGE,"E19");var subQ4=sQuery(id+"F9.wireOp",EDGE,"E15");var subQ5=makeQuery(id+"F25.opLoft","SWEPT_FACE",FACE,{"disambiguationData":[OSD([sQuery(id+"F3.wireOp",EDGE,"E9.MirrorCS"),subQ4,subQ3,subQ2,subQ1])]});var subQ6=makeQuery(id+"F36.opExtrude","SWEPT_FACE",FACE,{"disambiguationData":[OSD([sQuery(id+"F35.wireOp",EDGE,"E54")])]});Q1=makeQuery(id+"F38.boolean.opBoolean","SPLIT",FACE,{"disambiguationData":[TD([makeQuery(id+"F13.opLoft","SWEPT_FACE",FACE,{"disambiguationData":[OSD([sQuery(id+"F3.wireOp",EDGE,"E8"),subQ4,subQ3,sQuery(id+"F11.wireOp",EDGE,"E20"),sQuery(id+"F12.wireOp",EDGE,"E22")])]}),subQ5,makeQuery(id+"F27.opLoft","SWEPT_FACE",FACE,{"disambiguationData":[OSD([subQ2,subQ1,sQuery(id+"F24.wireOp",EDGE,"E44"),sQuery(id+"F26.wireOp",EDGE,"E45")])]}),subQ0,subQ6,makeQuery(id+"F38.opPattern","COPY",FACE,{"derivedFrom":subQ0,"instanceName":"1"}),makeQuery(id+"F38.opPattern","COPY",FACE,{"derivedFrom":subQ6,"instanceName":"1"})])],"derivedFrom":subQ5});}
            extrude(context, id + "F49", {"entities" : qUnion([Q0]), "operationType" : NewBodyOperationType.ADD, "endBound" : BoundingType.UP_TO_SURFACE, "endBoundEntityFace" : qUnion([Q1]), "depth" : 25 * mm});
        }
        {
            var Q0;
            Q0=qCreatedBy(makeId("Top.planeOp"),FACE);
            cPlane(context, id + "F50", {"entities" : qUnion([Q0]), "cplaneType" : CPlaneType.OFFSET, "offset" : 25 * mm, "width" : 150 * mm, "height" : 150 * mm});
        }
        {
            var Q0;
            Q0=qCreatedBy(id+"F50.planeOp",FACE);
            var sketch = newSketch(context, id + "F51", { "sketchPlane" : qUnion([Q0])});
            skLineSegment(sketch, "E65", {"start": v(0, 0) * mm, "end": v(0, 145) * mm, "construction": true});
            skFitSpline(sketch, "E66", {"points": [v(0, 145) * mm, v(-0.66, 146.79) * mm, v(0, 150) * mm], "startDerivative": vector(-4.26, 2.06) * mm, "endDerivative": vector(2.38, 11.26) * mm});
            skFitSpline(sketch, "E67.MirrorCS", {"points": [v(0, 145) * mm, v(0.66, 146.79) * mm, v(0, 150) * mm], "startDerivative": vector(4.26, 2.06) * mm, "endDerivative": vector(-2.38, 11.26) * mm});
            skSolve(sketch);
        }
        {
            var Q0;
            Q0=qCreatedBy(makeId("Top.planeOp"),FACE);
            cPlane(context, id + "F52", {"entities" : qUnion([Q0]), "cplaneType" : CPlaneType.OFFSET, "offset" : 10 * mm, "width" : 150 * mm, "height" : 150 * mm});
        }
        {
            var Q0;
            Q0=qCreatedBy(id+"F52.planeOp",FACE);
            var sketch = newSketch(context, id + "F53", { "sketchPlane" : qUnion([Q0])});
            skLineSegment(sketch, "E68", {"start": v(0, 0) * mm, "end": v(0, 140) * mm, "construction": true});
            skPoint(sketch, "E69.0", {"position": v(0, 150) * mm});
            skFitSpline(sketch, "E70", {"points": [v(0, 140) * mm, v(-0.92, 142) * mm, v(0, 150) * mm], "startDerivative": vector(-6.44, 5.81) * mm, "endDerivative": vector(4.8, 27.45) * mm});
            skFitSpline(sketch, "E71.MirrorCS", {"points": [v(0, 140) * mm, v(0.92, 142) * mm, v(0, 150) * mm], "startDerivative": vector(6.44, 5.81) * mm, "endDerivative": vector(-4.8, 27.45) * mm});
            skSolve(sketch);
        }
        {
            var Q1;
            Q1=makeQuery(id+"F51.imprint","IMPRINT",FACE,{"disambiguationData":[TD([[makeQuery(id+"F51.imprint","IMPRINT",EDGE,{"derivedFrom":sQuery(id+"F51.wireOp",EDGE,"E66")}),-1.0]])]});
            var Q2;
            Q2 = qSketchRegion(id + "F53", true);
            loft(context, id + "F54", {"operationType" : NewBodyOperationType.ADD, "sheetProfilesArray" : [{ "sheetProfileEntities" : qUnion([Q1]) }, { "sheetProfileEntities" : qUnion([Q2]) }]});
        }
        {
            var Q0;
            {var subQ0=sQuery(id+"F53.wireOp",EDGE,"E71.MirrorCS");var subQ1=sQuery(id+"F53.wireOp",EDGE,"E70");var subQ2=sQuery(id+"F51.wireOp",EDGE,"E67.MirrorCS");var subQ3=sQuery(id+"F51.wireOp",EDGE,"E66");Q0=makeQuery(id+"F54.boolean.opBoolean","INTERSECT",EDGE,{"derivedFrom":[makeQuery(id+"F8.opLoft","SWEPT_FACE",FACE,{"disambiguationData":[OSD([sQuery(id+"F0.wireOp",EDGE,"E1"),sQuery(id+"F2.wireOp",EDGE,"E3"),sQuery(id+"F3.wireOp",EDGE,"E9.MirrorCS"),sQuery(id+"F5.wireOp",EDGE,"E10"),sQuery(id+"F7.wireOp",EDGE,"E12")])]}),makeQuery(id+"F54.opLoft","SWEPT_FACE",FACE,{"disambiguationData":[OSD([subQ3,subQ2,subQ1,subQ0]),TDD([makeQuery(id+"F51.imprint","INTERSECT",VERTEX,{"disambiguationData":[OD(0.0)],"derivedFrom":[subQ3,subQ2]}),makeQuery(id+"F51.imprint","INTERSECT",VERTEX,{"disambiguationData":[OD(1.0)],"derivedFrom":[subQ3,subQ2]}),makeQuery(id+"F51.imprint","IMPRINT",EDGE,{"derivedFrom":subQ2}),makeQuery(id+"F53.imprint","INTERSECT",VERTEX,{"disambiguationData":[OD(0.0)],"derivedFrom":[subQ1,subQ0]}),makeQuery(id+"F53.imprint","INTERSECT",VERTEX,{"disambiguationData":[OD(1.0)],"derivedFrom":[subQ1,subQ0]}),makeQuery(id+"F53.imprint","IMPRINT",EDGE,{"derivedFrom":subQ0})])]})]});}
            var Q1;
            {var subQ0=sQuery(id+"F53.wireOp",EDGE,"E70");var subQ1=sQuery(id+"F53.wireOp",EDGE,"E71.MirrorCS");var subQ2=sQuery(id+"F51.wireOp",EDGE,"E66");var subQ3=sQuery(id+"F51.wireOp",EDGE,"E67.MirrorCS");Q1=makeQuery(id+"F54.boolean.opBoolean","INTERSECT",EDGE,{"derivedFrom":[makeQuery(id+"F8.opLoft","SWEPT_FACE",FACE,{"disambiguationData":[OSD([sQuery(id+"F0.wireOp",EDGE,"E1"),sQuery(id+"F2.wireOp",EDGE,"E3"),sQuery(id+"F3.wireOp",EDGE,"E9.MirrorCS"),sQuery(id+"F5.wireOp",EDGE,"E10"),sQuery(id+"F7.wireOp",EDGE,"E12")])]}),makeQuery(id+"F54.opLoft","SWEPT_FACE",FACE,{"disambiguationData":[OSD([subQ2,subQ3,subQ0,subQ1]),TDD([makeQuery(id+"F51.imprint","INTERSECT",VERTEX,{"disambiguationData":[OD(0.0)],"derivedFrom":[subQ2,subQ3]}),makeQuery(id+"F51.imprint","INTERSECT",VERTEX,{"disambiguationData":[OD(1.0)],"derivedFrom":[subQ2,subQ3]}),makeQuery(id+"F51.imprint","IMPRINT",EDGE,{"derivedFrom":subQ2}),makeQuery(id+"F53.imprint","INTERSECT",VERTEX,{"disambiguationData":[OD(0.0)],"derivedFrom":[subQ0,subQ1]}),makeQuery(id+"F53.imprint","INTERSECT",VERTEX,{"disambiguationData":[OD(1.0)],"derivedFrom":[subQ0,subQ1]}),makeQuery(id+"F53.imprint","IMPRINT",EDGE,{"derivedFrom":subQ0})])]})]});}
            fillet(context, id + "F55", {"entities" : qUnion([Q0, Q1]), "radius" : 1 * mm, "tangentPropagation" : true, "allowEdgeOverflow" : false});
        }
    });
